# Revit family: LF-T16-S-RxX115-30xx-SI
name_source: partatom
category: Leuchten
units: mm (PartAtom-declared; Revit-internal decimal feet)

## family parameters
Basisbauteil = Fläche
Beim Laden mit Abzugskörper schneiden = Nein
Bemaßung runder Anschluss = Durchmesser verwenden
Gemeinsam genutzt = Nein
Lichtquelle = Ja
OmniClass-Nummer = 23.80.70.11
OmniClass-Titel = Luminaries for Internal Lighting
Raumberechnungspunkt = Nein
Teiletyp = Normal

## types (8) — shared parameters
Baugruppenkennzeichen = D5020200
Emissionsform beim Rendern sichtbar = Nein
Farbfilter = 16777215
Farbtemperaturverschiebung bei Dämpfen der Lampe = <Keine Auswahl>
Hersteller = RIDI Leuchten GmbH
Lampe = LED
Neigungswinkel = 90.00°
URL = www.ridi.de
Von Breite des Rechtecks ausssenden = 1200 mm
Von Länge des Rechtecks aussenden = 85 mm  [stored 0.278871 ft]
brand = RIDI
conformity mark = CE
electrical safety class = 1
height = 72 mm  [stored 0.23622 ft]
ingress protection (IP) code = IP64
length = 1198 mm  [stored 3.93045 ft]
nominal frequency = 50-60Hz
nominal voltage = 230
voltage type (AC, DC, UC) = AC
width = 85 mm  [stored 0.278871 ft]
zero-valued in all types: Vorgabe-Ansicht

## per-type parameters (varying)
| type | Datei für fotometrisches Netz | Modell | Scheinlast | rated input power | weight |
| LF-T16-S-R1X115/30ND-SM SI | LF-T16-S-R1xxx-SM.IES | 0450020SI | 35 VA | 35 | 2.66 kg |
| LF-T16-S-R1X115/30DA-SM SI | LF-T16-S-R1xxx-SM.IES | 0460020SI | 35 VA | 35 | 2.66 kg |
| LF-T16-S-R1X115/30ND-OE SI | LF-T16-S-R1xxx-OE.IES | 0450006SI | 35 VA | 35 | 2,55 kg |
| LF-T16-S-R1X115/30DA-OE SI | LF-T16-S-R1xxx-OE.IES | 0460006SI | 35 VA | 35 | 2,55 kg |
| LF-T16-S-R2X115/30ND-OE SI | LF-T16-S-R2xxx-OE.IES | 0450063SI | 70 VA | 70 | 3,17 kg |
| LF-T16-S-R2X115/30DA-OE SI | LF-T16-S-R2xxx-OE.IES | 0460063SI | 70 VA | 70 | 3,17 kg |
| LF-T16-S-R1X115/30ND-AS SI | LF-T16-S-R1xxx-AS.IES | 0450022SI | 35 VA | 35 | 2,49 kg |
| LF-T16-S-R1X115/30DA-AS SI | LF-T16-S-R1xxx-AS.IES | 0460022SI | 35 VA | 35 | 2,49 kg |

note: column(s) folded — value = type name in every type: product name

note: [stored X ft] marks values corroborated as IEEE doubles in the binary element streams (Revit-internal decimal feet)
